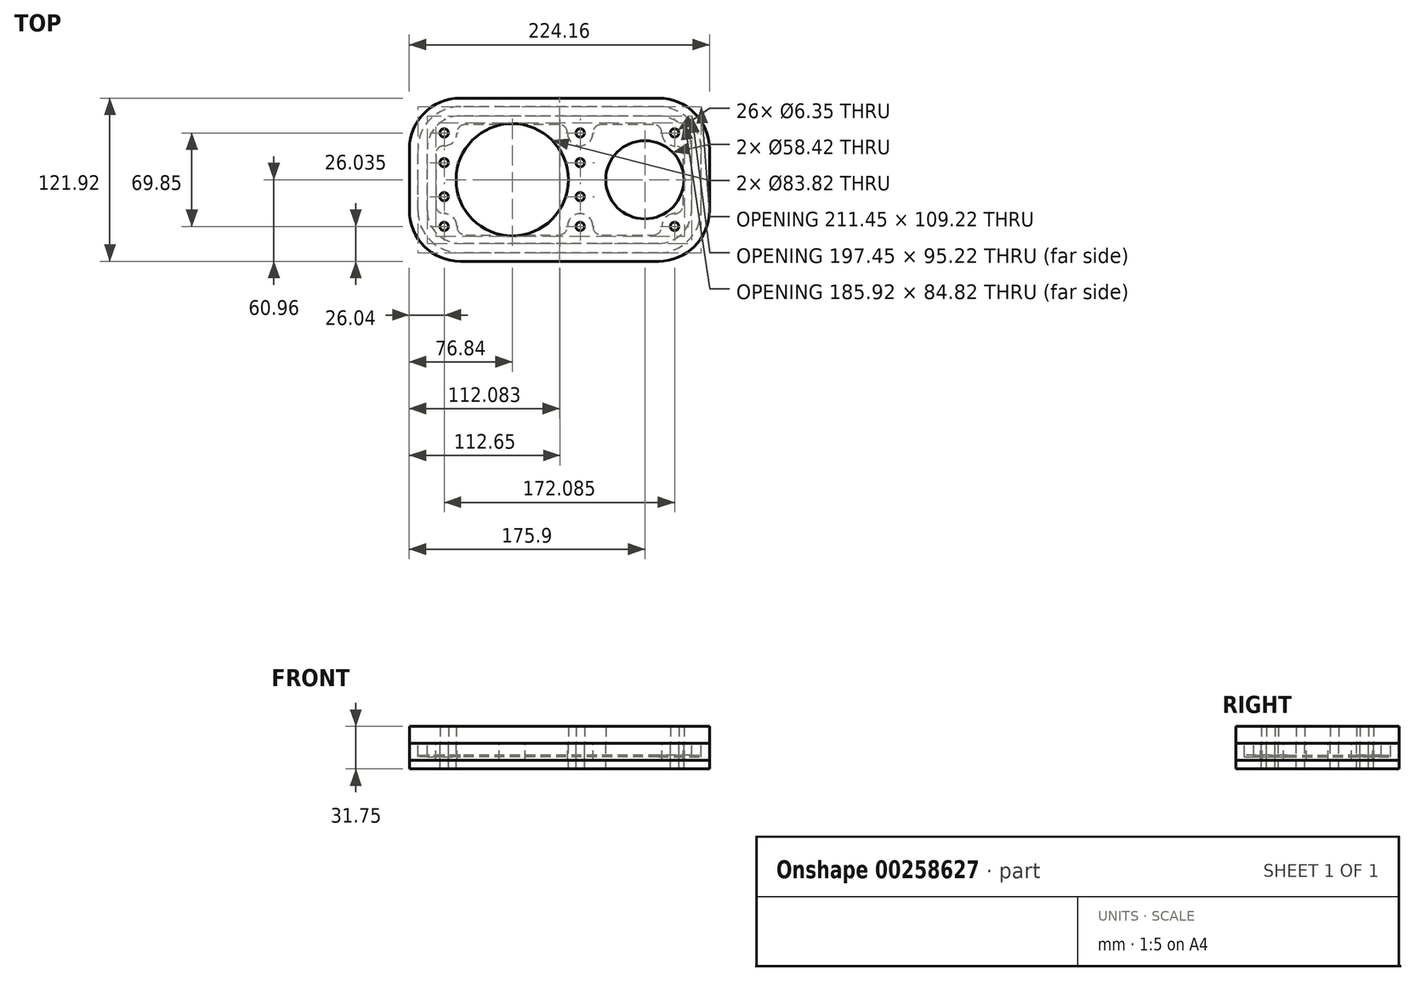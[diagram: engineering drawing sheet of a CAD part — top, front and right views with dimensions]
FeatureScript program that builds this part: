
annotation { "Feature Type Name" : "Feature", "Feature Type Description" : "" }
export const myFeature = defineFeature(function(context is Context, id is Id, definition is map)
    precondition{}
    {
        {
            var Q0;
            Q0=qCreatedBy(makeId("Top.planeOp"),FACE);
            var sketch = newSketch(context, id + "F0", { "sketchPlane" : qUnion([Q0])});
            skLineSegment(sketch, "E0.bottom", {"start": v(50.8, -12.7) * mm, "end": v(-50.8, -12.7) * mm, "construction": true});
            skLineSegment(sketch, "E0.top", {"start": v(50.8, 12.7) * mm, "end": v(-50.8, 12.7) * mm, "construction": true});
            skLineSegment(sketch, "E0.left", {"start": v(50.8, -12.7) * mm, "end": v(50.8, 12.7) * mm, "construction": true});
            skLineSegment(sketch, "E0.right", {"start": v(-50.8, -12.7) * mm, "end": v(-50.8, 12.7) * mm, "construction": true});
            skPoint(sketch, "E0.middle", {"position": v(0, 0) * mm});
            skCircle(sketch, "E1", {"center": v(0, 0) * mm, "radius": 41.91 * mm});
            skCircle(sketch, "E2", {"center": v(-50.8, 12.7) * mm, "radius": 3.18 * mm});
            skCircle(sketch, "E3", {"center": v(-50.8, -12.7) * mm, "radius": 3.18 * mm});
            skCircle(sketch, "E4", {"center": v(50.8, -12.7) * mm, "radius": 3.18 * mm});
            skCircle(sketch, "E5", {"center": v(50.8, 12.7) * mm, "radius": 3.18 * mm});
            skLineSegment(sketch, "E6.1", {"start": v(147.32, -22.86) * mm, "end": v(147.32, 22.86) * mm});
            skLineSegment(sketch, "E6.2", {"start": v(109.22, -60.96) * mm, "end": v(-38.74, -60.96) * mm});
            skLineSegment(sketch, "E6.5", {"start": v(-76.84, -22.86) * mm, "end": v(-76.84, 22.86) * mm});
            skLineSegment(sketch, "E6.7", {"start": v(109.22, 60.96) * mm, "end": v(-38.74, 60.96) * mm});
            skLineSegment(sketch, "E7", {"start": v(0, 0) * mm, "end": v(99.06, 0) * mm});
            skCircle(sketch, "E8", {"center": v(99.06, 0) * mm, "radius": 29.21 * mm});
            skPoint(sketch, "E9.visualSharp", {"position": v(-76.84, 60.96) * mm});
            skArc(sketch, "E9.filletArc", {"start": v(-38.74, 60.96) * mm, "mid": v(-65.68, 49.8) * mm, "end": v(-76.84, 22.86) * mm});
            skPoint(sketch, "E10.visualSharp", {"position": v(-76.84, -60.96) * mm});
            skArc(sketch, "E10.filletArc", {"start": v(-76.84, -22.86) * mm, "mid": v(-65.68, -49.8) * mm, "end": v(-38.74, -60.96) * mm});
            skPoint(sketch, "E11.visualSharp", {"position": v(147.32, -60.96) * mm});
            skArc(sketch, "E11.filletArc", {"start": v(109.22, -60.96) * mm, "mid": v(136.16, -49.8) * mm, "end": v(147.32, -22.86) * mm});
            skPoint(sketch, "E12.visualSharp", {"position": v(147.32, 60.96) * mm});
            skArc(sketch, "E12.filletArc", {"start": v(147.32, 22.86) * mm, "mid": v(136.16, 49.8) * mm, "end": v(109.22, 60.96) * mm});
            skArc(sketch, "E13.0", {"start": v(109.22, -54.61) * mm, "mid": v(131.67, -45.31) * mm, "end": v(140.97, -22.86) * mm});
            skLineSegment(sketch, "E13.1", {"start": v(140.97, -22.86) * mm, "end": v(140.97, 22.86) * mm});
            skLineSegment(sketch, "E13.2", {"start": v(109.22, -54.6) * mm, "end": v(-38.74, -54.61) * mm});
            skArc(sketch, "E13.3", {"start": v(140.97, 22.86) * mm, "mid": v(131.67, 45.31) * mm, "end": v(109.22, 54.61) * mm});
            skArc(sketch, "E13.4", {"start": v(-70.49, -22.86) * mm, "mid": v(-61.19, -45.31) * mm, "end": v(-38.74, -54.6) * mm});
            skLineSegment(sketch, "E13.5", {"start": v(-70.49, -22.86) * mm, "end": v(-70.49, 22.86) * mm});
            skArc(sketch, "E13.6", {"start": v(-38.74, 54.6) * mm, "mid": v(-61.19, 45.31) * mm, "end": v(-70.49, 22.86) * mm});
            skLineSegment(sketch, "E13.7", {"start": v(109.22, 54.61) * mm, "end": v(-38.74, 54.6) * mm});
            skArc(sketch, "E14.0", {"start": v(109.22, -47.61) * mm, "mid": v(126.72, -40.36) * mm, "end": v(133.97, -22.86) * mm});
            skLineSegment(sketch, "E14.1", {"start": v(133.97, -22.86) * mm, "end": v(133.97, 22.86) * mm});
            skLineSegment(sketch, "E14.2", {"start": v(109.22, -47.6) * mm, "end": v(-38.74, -47.61) * mm});
            skArc(sketch, "E14.3", {"start": v(133.97, 22.86) * mm, "mid": v(126.72, 40.36) * mm, "end": v(109.22, 47.61) * mm});
            skArc(sketch, "E14.4", {"start": v(-63.49, -22.86) * mm, "mid": v(-56.24, -40.36) * mm, "end": v(-38.74, -47.6) * mm});
            skLineSegment(sketch, "E14.5", {"start": v(-63.49, -22.86) * mm, "end": v(-63.49, 22.86) * mm});
            skArc(sketch, "E14.6", {"start": v(-38.74, 47.6) * mm, "mid": v(-56.24, 40.36) * mm, "end": v(-63.49, 22.86) * mm});
            skLineSegment(sketch, "E14.7", {"start": v(109.22, 47.61) * mm, "end": v(-38.74, 47.6) * mm});
            skCircle(sketch, "E15", {"center": v(-50.8, 34.93) * mm, "radius": 3.18 * mm});
            skCircle(sketch, "E16", {"center": v(50.8, 34.93) * mm, "radius": 3.18 * mm});
            skCircle(sketch, "E17", {"center": v(121.29, 34.93) * mm, "radius": 3.18 * mm});
            skCircle(sketch, "E18", {"center": v(121.29, -34.93) * mm, "radius": 3.18 * mm});
            skCircle(sketch, "E19", {"center": v(50.8, -34.93) * mm, "radius": 3.18 * mm});
            skCircle(sketch, "E20", {"center": v(-50.8, -34.93) * mm, "radius": 3.18 * mm});
            skLineSegment(sketch, "E21", {"start": v(0, 41.91) * mm, "end": v(0, 60.96) * mm, "construction": true});
            skLineSegment(sketch, "E22", {"start": v(128.27, 0) * mm, "end": v(147.32, 0) * mm, "construction": true});
            skLineSegment(sketch, "E23", {"start": v(0, -41.91) * mm, "end": v(0, -60.96) * mm, "construction": true});
            skPoint(sketch, "E24", {"position": v(41.91, 0) * mm});
            skPoint(sketch, "E25", {"position": v(69.85, 0) * mm});
            skSolve(sketch);
        }
        {
            var Q0;
            Q0=makeQuery(id+"F0.imprint","IMPRINT",FACE,{"disambiguationData":[TD([[makeQuery(id+"F0.imprint","IMPRINT",EDGE,{"derivedFrom":sQuery(id+"F0.wireOp",EDGE,"E1")}),-1.0]])]});
            var Q1;
            Q1=makeQuery(id+"F0.imprint","IMPRINT",FACE,{"disambiguationData":[TD([[makeQuery(id+"F0.imprint","IMPRINT",EDGE,{"derivedFrom":sQuery(id+"F0.wireOp",EDGE,"E13.0")}),1.0]])]});
            var Q2;
            Q2=makeQuery(id+"F0.imprint","IMPRINT",FACE,{"disambiguationData":[TD([[makeQuery(id+"F0.imprint","IMPRINT",EDGE,{"derivedFrom":sQuery(id+"F0.wireOp",EDGE,"E6.1")}),1.0]])]});
            extrude(context, id + "F1", {"entities" : qUnion([Q0, Q1, Q2]), "oppositeDirection" : true, "depth" : 19.05 * mm});
        }
        {
            var Q0;
            Q0=makeQuery(id+"F0.imprint","IMPRINT",FACE,{"disambiguationData":[TD([[makeQuery(id+"F0.imprint","IMPRINT",EDGE,{"derivedFrom":sQuery(id+"F0.wireOp",EDGE,"E13.0")}),1.0]])]});
            extrude(context, id + "F2", {"entities" : qUnion([Q0]), "operationType" : NewBodyOperationType.REMOVE, "oppositeDirection" : true, "depth" : 10 * mm});
        }
        {
            var Q0;
            Q0=qCreatedBy(makeId("Top.planeOp"),FACE);
            var sketch = newSketch(context, id + "F3", { "sketchPlane" : qUnion([Q0])});
            skPoint(sketch, "E26.0", {"position": v(-50.8, 34.93) * mm});
            skPoint(sketch, "E27.0", {"position": v(-50.8, -34.93) * mm});
            skPoint(sketch, "E28.0", {"position": v(-50.8, 12.7) * mm});
            skPoint(sketch, "E29.0", {"position": v(-50.8, -12.7) * mm});
            skPoint(sketch, "E30.0", {"position": v(0, 0) * mm});
            skPoint(sketch, "E31.0", {"position": v(50.8, 34.93) * mm});
            skPoint(sketch, "E32.0", {"position": v(50.8, 12.7) * mm});
            skPoint(sketch, "E33.0", {"position": v(50.8, -12.7) * mm});
            skPoint(sketch, "E34.0", {"position": v(50.8, -34.93) * mm});
            skPoint(sketch, "E35.0", {"position": v(99.06, 0) * mm});
            skPoint(sketch, "E36.0", {"position": v(121.29, 34.93) * mm});
            skPoint(sketch, "E37.0", {"position": v(121.29, -34.93) * mm});
            skPoint(sketch, "E38.0", {"position": v(109.22, -22.86) * mm});
            skPoint(sketch, "E39.0", {"position": v(109.22, -60.96) * mm});
            skPoint(sketch, "E40.0", {"position": v(147.32, -22.86) * mm});
            skPoint(sketch, "E41.0", {"position": v(147.32, 22.86) * mm});
            skPoint(sketch, "E42.0", {"position": v(109.22, 60.96) * mm});
            skPoint(sketch, "E43.0", {"position": v(-38.74, 60.96) * mm});
            skPoint(sketch, "E44.0", {"position": v(-76.84, 22.86) * mm});
            skPoint(sketch, "E45.0", {"position": v(-76.84, -22.86) * mm});
            skPoint(sketch, "E46.0", {"position": v(-38.74, -60.96) * mm});
            skPoint(sketch, "E47.0", {"position": v(-38.74, 22.86) * mm});
            skPoint(sketch, "E48.0", {"position": v(-38.74, -22.86) * mm});
            skArc(sketch, "E49", {"start": v(-38.74, 60.96) * mm, "mid": v(-65.68, 49.8) * mm, "end": v(-76.84, 22.86) * mm});
            skArc(sketch, "E50", {"start": v(-76.84, -22.86) * mm, "mid": v(-65.68, -49.8) * mm, "end": v(-38.74, -60.96) * mm});
            skArc(sketch, "E51", {"start": v(109.22, -60.96) * mm, "mid": v(136.16, -49.8) * mm, "end": v(147.32, -22.86) * mm});
            skPoint(sketch, "E52.0", {"position": v(109.22, 22.86) * mm});
            skArc(sketch, "E53", {"start": v(147.32, 22.86) * mm, "mid": v(136.16, 49.8) * mm, "end": v(109.22, 60.96) * mm});
            skLineSegment(sketch, "E54", {"start": v(-38.74, 60.96) * mm, "end": v(109.22, 60.96) * mm});
            skLineSegment(sketch, "E55", {"start": v(147.32, 22.86) * mm, "end": v(147.32, -22.86) * mm});
            skLineSegment(sketch, "E56", {"start": v(109.22, -60.96) * mm, "end": v(-38.74, -60.96) * mm});
            skLineSegment(sketch, "E57", {"start": v(-76.84, -22.86) * mm, "end": v(-76.84, 22.86) * mm});
            skPoint(sketch, "E58.0", {"position": v(41.91, 0) * mm});
            skPoint(sketch, "E59.0", {"position": v(69.85, 0) * mm});
            skCircle(sketch, "E60", {"center": v(0, 0) * mm, "radius": 41.91 * mm});
            skCircle(sketch, "E61", {"center": v(99.06, 0) * mm, "radius": 29.21 * mm});
            skCircle(sketch, "E62", {"center": v(-50.8, 34.93) * mm, "radius": 3.18 * mm});
            skCircle(sketch, "E63", {"center": v(-50.8, 12.7) * mm, "radius": 3.18 * mm});
            skCircle(sketch, "E64", {"center": v(-50.8, -12.7) * mm, "radius": 3.17 * mm});
            skCircle(sketch, "E65", {"center": v(-50.8, -34.93) * mm, "radius": 3.17 * mm});
            skCircle(sketch, "E66", {"center": v(50.8, -34.93) * mm, "radius": 3.18 * mm});
            skCircle(sketch, "E67", {"center": v(50.8, -12.7) * mm, "radius": 3.18 * mm});
            skCircle(sketch, "E68", {"center": v(50.8, 12.7) * mm, "radius": 3.18 * mm});
            skCircle(sketch, "E69", {"center": v(50.8, 34.93) * mm, "radius": 3.18 * mm});
            skCircle(sketch, "E70", {"center": v(121.29, 34.93) * mm, "radius": 3.18 * mm});
            skCircle(sketch, "E71", {"center": v(121.29, -34.93) * mm, "radius": 3.18 * mm});
            skSolve(sketch);
        }
        {
            var Q0;
            Q0=qCreatedBy(makeId("Top.planeOp"),FACE);
            var sketch = newSketch(context, id + "F4", { "sketchPlane" : qUnion([Q0])});
            skPoint(sketch, "E72.0", {"position": v(-38.74, 22.86) * mm});
            skPoint(sketch, "E73.0", {"position": v(-38.74, -22.86) * mm});
            skPoint(sketch, "E74.0", {"position": v(-38.74, -60.96) * mm});
            skPoint(sketch, "E75.0", {"position": v(-38.74, -54.61) * mm});
            skPoint(sketch, "E76.0", {"position": v(-38.74, -47.61) * mm});
            skPoint(sketch, "E77.0", {"position": v(-63.49, -22.86) * mm});
            skPoint(sketch, "E78.0", {"position": v(-70.49, -22.86) * mm});
            skPoint(sketch, "E79.0", {"position": v(-76.84, -22.86) * mm});
            skPoint(sketch, "E80.0", {"position": v(-76.84, 22.86) * mm});
            skPoint(sketch, "E81.0", {"position": v(-70.49, 22.86) * mm});
            skPoint(sketch, "E82.0", {"position": v(-63.49, 22.86) * mm});
            skPoint(sketch, "E83.0", {"position": v(-38.74, 47.6) * mm});
            skPoint(sketch, "E84.0", {"position": v(-38.74, 54.6) * mm});
            skPoint(sketch, "E85.0", {"position": v(-38.74, 60.96) * mm});
            skPoint(sketch, "E86.0", {"position": v(109.22, 60.96) * mm});
            skPoint(sketch, "E87.0", {"position": v(109.22, 54.61) * mm});
            skPoint(sketch, "E88.0", {"position": v(109.22, 47.61) * mm});
            skPoint(sketch, "E89.0", {"position": v(109.22, 22.86) * mm});
            skPoint(sketch, "E90.0", {"position": v(133.97, 22.86) * mm});
            skPoint(sketch, "E91.0", {"position": v(140.97, 22.86) * mm});
            skPoint(sketch, "E92.0", {"position": v(147.32, 22.86) * mm});
            skPoint(sketch, "E93.0", {"position": v(147.32, -22.86) * mm});
            skPoint(sketch, "E94.0", {"position": v(140.97, -22.86) * mm});
            skPoint(sketch, "E95.0", {"position": v(133.97, -22.86) * mm});
            skPoint(sketch, "E96.0", {"position": v(109.22, -47.6) * mm});
            skPoint(sketch, "E97.0", {"position": v(109.22, -54.6) * mm});
            skPoint(sketch, "E98.0", {"position": v(109.22, -60.96) * mm});
            skPoint(sketch, "E99.0", {"position": v(-50.8, 34.93) * mm});
            skPoint(sketch, "E100.0", {"position": v(-50.8, -34.93) * mm});
            skPoint(sketch, "E101.0", {"position": v(50.8, -34.93) * mm});
            skPoint(sketch, "E102.0", {"position": v(50.8, 34.93) * mm});
            skPoint(sketch, "E103.0", {"position": v(121.29, 34.93) * mm});
            skPoint(sketch, "E104.0", {"position": v(121.29, -34.93) * mm});
            skArc(sketch, "E105", {"start": v(-38.74, 47.6) * mm, "mid": v(-56.24, 40.36) * mm, "end": v(-63.49, 22.86) * mm});
            skArc(sketch, "E106", {"start": v(-38.74, 54.61) * mm, "mid": v(-61.19, 45.31) * mm, "end": v(-70.49, 22.86) * mm});
            skArc(sketch, "E107", {"start": v(-38.74, 60.96) * mm, "mid": v(-65.68, 49.8) * mm, "end": v(-76.84, 22.86) * mm});
            skArc(sketch, "E108", {"start": v(-63.49, -22.86) * mm, "mid": v(-56.24, -40.36) * mm, "end": v(-38.74, -47.6) * mm});
            skArc(sketch, "E109", {"start": v(-70.48, -22.86) * mm, "mid": v(-61.19, -45.31) * mm, "end": v(-38.74, -54.6) * mm});
            skArc(sketch, "E110", {"start": v(-76.84, -22.86) * mm, "mid": v(-65.68, -49.8) * mm, "end": v(-38.74, -60.96) * mm});
            skPoint(sketch, "E111.0", {"position": v(109.22, -22.86) * mm});
            skArc(sketch, "E112", {"start": v(133.97, -22.86) * mm, "mid": v(126.72, -40.36) * mm, "end": v(109.22, -47.61) * mm});
            skArc(sketch, "E113", {"start": v(140.97, -22.86) * mm, "mid": v(131.67, -45.31) * mm, "end": v(109.22, -54.61) * mm});
            skArc(sketch, "E114", {"start": v(147.32, -22.86) * mm, "mid": v(136.16, -49.8) * mm, "end": v(109.22, -60.96) * mm});
            skArc(sketch, "E115", {"start": v(133.97, 22.86) * mm, "mid": v(126.72, 40.36) * mm, "end": v(109.22, 47.61) * mm});
            skArc(sketch, "E116", {"start": v(140.97, 22.86) * mm, "mid": v(131.67, 45.31) * mm, "end": v(109.22, 54.61) * mm});
            skArc(sketch, "E117", {"start": v(147.32, 22.86) * mm, "mid": v(136.16, 49.8) * mm, "end": v(109.22, 60.96) * mm});
            skLineSegment(sketch, "E118", {"start": v(109.22, 47.61) * mm, "end": v(-38.74, 47.6) * mm});
            skLineSegment(sketch, "E119", {"start": v(-38.74, 54.6) * mm, "end": v(109.22, 54.61) * mm});
            skLineSegment(sketch, "E120", {"start": v(109.22, 60.96) * mm, "end": v(-38.74, 60.96) * mm});
            skLineSegment(sketch, "E121", {"start": v(-63.49, 22.86) * mm, "end": v(-63.49, -22.86) * mm});
            skLineSegment(sketch, "E122", {"start": v(-70.49, -22.86) * mm, "end": v(-70.49, 22.86) * mm});
            skLineSegment(sketch, "E123", {"start": v(-76.84, 22.86) * mm, "end": v(-76.84, -22.86) * mm});
            skLineSegment(sketch, "E124", {"start": v(-38.74, -47.61) * mm, "end": v(109.22, -47.6) * mm});
            skLineSegment(sketch, "E125", {"start": v(109.22, -54.6) * mm, "end": v(-38.74, -54.6) * mm});
            skLineSegment(sketch, "E126", {"start": v(-38.74, -60.96) * mm, "end": v(109.22, -60.96) * mm});
            skLineSegment(sketch, "E127", {"start": v(133.97, -22.86) * mm, "end": v(133.97, 22.86) * mm});
            skLineSegment(sketch, "E128", {"start": v(140.97, -22.86) * mm, "end": v(140.97, 22.86) * mm});
            skLineSegment(sketch, "E129", {"start": v(147.32, -22.86) * mm, "end": v(147.32, 22.86) * mm});
            skPoint(sketch, "E130.0", {"position": v(-50.8, -12.7) * mm});
            skPoint(sketch, "E131.0", {"position": v(-50.8, 12.7) * mm});
            skPoint(sketch, "E132.0", {"position": v(50.8, -12.7) * mm});
            skPoint(sketch, "E133.0", {"position": v(50.8, 12.7) * mm});
            skArc(sketch, "E134", {"start": v(-50.8, 25.4) * mm, "mid": v(-44.06, 28.19) * mm, "end": v(-41.28, 34.93) * mm});
            skArc(sketch, "E135", {"start": v(-50.8, 25.4) * mm, "mid": v(-55.3, 23.54) * mm, "end": v(-57.15, 19.05) * mm});
            skArc(sketch, "E136", {"start": v(-41.28, -34.93) * mm, "mid": v(-44.06, -28.19) * mm, "end": v(-50.8, -25.4) * mm});
            skArc(sketch, "E137", {"start": v(-41.28, -34.93) * mm, "mid": v(-39.42, -39.42) * mm, "end": v(-34.93, -41.28) * mm});
            skArc(sketch, "E138", {"start": v(34.93, -41.28) * mm, "mid": v(39.42, -39.42) * mm, "end": v(41.28, -34.93) * mm});
            skArc(sketch, "E139", {"start": v(60.33, -34.93) * mm, "mid": v(50.8, -25.4) * mm, "end": v(41.28, -34.93) * mm});
            skArc(sketch, "E140", {"start": v(60.33, -34.93) * mm, "mid": v(62.18, -39.42) * mm, "end": v(66.68, -41.28) * mm});
            skArc(sketch, "E141", {"start": v(105.41, -41.27) * mm, "mid": v(109.9, -39.42) * mm, "end": v(111.76, -34.92) * mm});
            skArc(sketch, "E142", {"start": v(121.29, -25.4) * mm, "mid": v(114.55, -28.19) * mm, "end": v(111.76, -34.92) * mm});
            skArc(sketch, "E143", {"start": v(121.29, -25.4) * mm, "mid": v(125.78, -23.54) * mm, "end": v(127.64, -19.05) * mm});
            skArc(sketch, "E144", {"start": v(127.64, 19.05) * mm, "mid": v(125.78, 23.54) * mm, "end": v(121.29, 25.4) * mm});
            skArc(sketch, "E145", {"start": v(111.76, 34.93) * mm, "mid": v(114.55, 28.19) * mm, "end": v(121.29, 25.4) * mm});
            skArc(sketch, "E146", {"start": v(111.76, 34.93) * mm, "mid": v(109.9, 39.42) * mm, "end": v(105.41, 41.28) * mm});
            skArc(sketch, "E147", {"start": v(66.68, 41.28) * mm, "mid": v(62.18, 39.42) * mm, "end": v(60.33, 34.93) * mm});
            skArc(sketch, "E148", {"start": v(-34.93, 41.28) * mm, "mid": v(-39.42, 39.42) * mm, "end": v(-41.28, 34.93) * mm});
            skArc(sketch, "E149", {"start": v(41.28, 34.93) * mm, "mid": v(50.8, 25.4) * mm, "end": v(60.33, 34.93) * mm});
            skArc(sketch, "E150", {"start": v(41.28, 34.93) * mm, "mid": v(39.42, 39.42) * mm, "end": v(34.93, 41.28) * mm});
            skArc(sketch, "E151", {"start": v(-57.15, -19.05) * mm, "mid": v(-55.3, -23.54) * mm, "end": v(-50.8, -25.4) * mm});
            skLineSegment(sketch, "E152", {"start": v(-57.15, 19.05) * mm, "end": v(-57.15, -19.05) * mm});
            skLineSegment(sketch, "E153", {"start": v(-34.93, -41.28) * mm, "end": v(-9.75, -41.28) * mm});
            skLineSegment(sketch, "E154", {"start": v(66.68, -41.28) * mm, "end": v(105.41, -41.28) * mm});
            skLineSegment(sketch, "E155", {"start": v(127.64, -19.05) * mm, "end": v(127.64, -8.13) * mm});
            skLineSegment(sketch, "E156", {"start": v(105.41, 41.28) * mm, "end": v(66.68, 41.28) * mm});
            skLineSegment(sketch, "E157", {"start": v(34.93, 41.28) * mm, "end": v(9.75, 41.28) * mm});
            skCircle(sketch, "E158", {"center": v(-50.8, 34.93) * mm, "radius": 3.18 * mm});
            skCircle(sketch, "E159", {"center": v(-50.8, -34.93) * mm, "radius": 3.18 * mm});
            skCircle(sketch, "E160", {"center": v(50.8, -34.93) * mm, "radius": 3.18 * mm});
            skCircle(sketch, "E161", {"center": v(50.8, 34.93) * mm, "radius": 3.18 * mm});
            skCircle(sketch, "E162", {"center": v(121.29, 34.93) * mm, "radius": 3.18 * mm});
            skCircle(sketch, "E163", {"center": v(121.29, -34.93) * mm, "radius": 3.18 * mm});
            skCircle(sketch, "E164.0", {"center": v(99.06, 0) * mm, "radius": 29.21 * mm});
            skPoint(sketch, "E165.0", {"position": v(0, 0) * mm});
            skCircle(sketch, "E166.0", {"center": v(0, 0) * mm, "radius": 41.91 * mm});
            skArc(sketch, "E167", {"start": v(-9.75, -41.28) * mm, "mid": v(0, -42.41) * mm, "end": v(9.75, -41.28) * mm});
            skArc(sketch, "E168", {"start": v(127.64, -8.13) * mm, "mid": v(128.77, 0) * mm, "end": v(127.64, 8.13) * mm});
            skArc(sketch, "E169.trimOffspring", {"start": v(9.75, 41.28) * mm, "mid": v(0, 42.41) * mm, "end": v(-9.75, 41.28) * mm});
            skLineSegment(sketch, "E170", {"start": v(-9.75, 41.28) * mm, "end": v(-34.93, 41.28) * mm});
            skLineSegment(sketch, "E171", {"start": v(9.75, 41.28) * mm, "end": v(-9.75, 41.28) * mm, "construction": true});
            skLineSegment(sketch, "E172", {"start": v(-9.75, -41.28) * mm, "end": v(9.75, -41.28) * mm, "construction": true});
            skLineSegment(sketch, "E173", {"start": v(9.75, -41.28) * mm, "end": v(34.93, -41.28) * mm});
            skLineSegment(sketch, "E174", {"start": v(127.64, 8.13) * mm, "end": v(127.64, 19.05) * mm});
            skLineSegment(sketch, "E175", {"start": v(127.64, -8.13) * mm, "end": v(127.64, 8.13) * mm, "construction": true});
            skSolve(sketch);
        }
        {
            var Q0;
            Q0=qSketchRegion(id+"F3",true);
            extrude(context, id + "F5", {"entities" : qUnion([Q0]), "depth" : 12.7 * mm});
        }
        {
            var Q0;
            Q0=qSketchRegion(id+"F4",true);
            var Q1;
            Q1=makeQuery(id+"F4.imprint","IMPRINT",FACE,{"disambiguationData":[TD([[makeQuery(id+"F4.imprint","IMPRINT",EDGE,{"derivedFrom":sQuery(id+"F4.wireOp",EDGE,"E105")}),-1.0]])]});
            var Q2;
            Q2=makeQuery(id+"F4.imprint","IMPRINT",FACE,{"disambiguationData":[TD([[makeQuery(id+"F4.imprint","IMPRINT",EDGE,{"derivedFrom":sQuery(id+"F4.wireOp",EDGE,"E105")}),1.0]])]});
            extrude(context, id + "F6", {"entities" : qUnion([Q0, Q1, Q2]), "oppositeDirection" : true, "depth" : 12.7 * mm});
        }
        {
            var Q0;
            Q0=makeQuery(id+"F4.imprint","IMPRINT",FACE,{"disambiguationData":[TD([[makeQuery(id+"F4.imprint","IMPRINT",EDGE,{"derivedFrom":sQuery(id+"F4.wireOp",EDGE,"E105")}),-1.0]])]});
            extrude(context, id + "F7", {"entities" : qUnion([Q0]), "operationType" : NewBodyOperationType.REMOVE, "oppositeDirection" : true, "depth" : 8.9 * mm});
        }
    });
